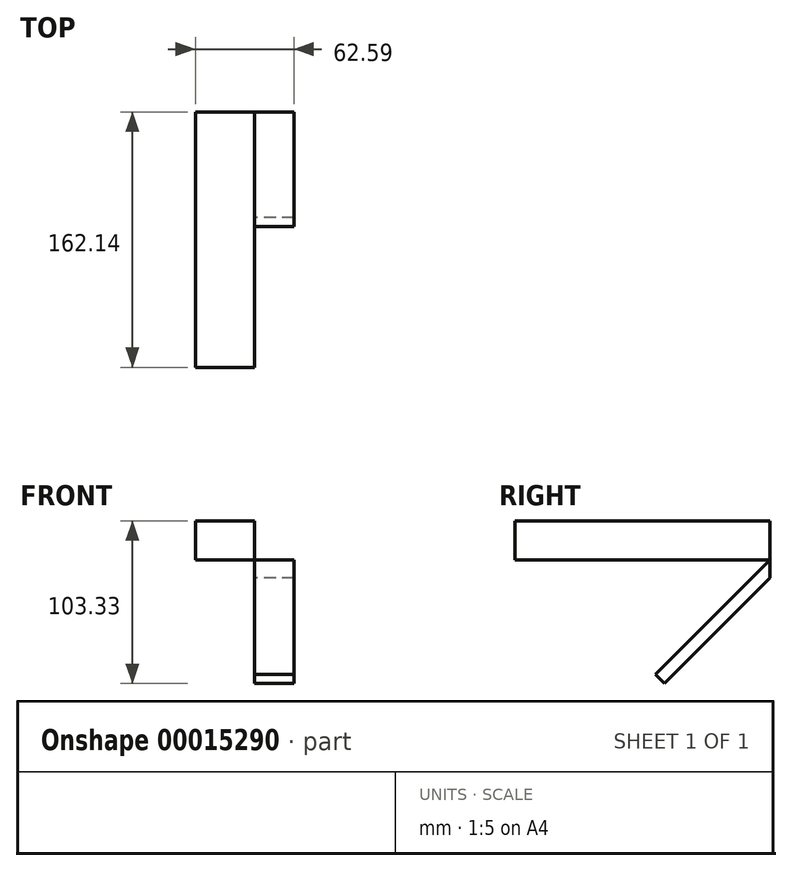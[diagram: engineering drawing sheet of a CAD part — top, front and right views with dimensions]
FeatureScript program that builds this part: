
annotation { "Feature Type Name" : "Feature", "Feature Type Description" : "" }
export const myFeature = defineFeature(function(context is Context, id is Id, definition is map)
    precondition{}
    {
        {
            var Q0;
            Q0=qCreatedBy(makeId("Right.planeOp"),FACE);
            var sketch = newSketch(context, id + "F0", { "sketchPlane" : qUnion([Q0])});
            skLineSegment(sketch, "E0", {"start": v(0, 0) * mm, "end": v(-55, -55) * mm});
            skLineSegment(sketch, "E1", {"start": v(0, -11.31) * mm, "end": v(-49.34, -60.66) * mm});
            skLineSegment(sketch, "E2", {"start": v(-55, -55) * mm, "end": v(-49.34, -60.66) * mm});
            skLineSegment(sketch, "E3", {"start": v(0, 0) * mm, "end": v(0, -11.31) * mm});
            skLineSegment(sketch, "E4", {"start": v(0, 0) * mm, "end": v(-66.64, -66.64) * mm, "construction": true});
            skSolve(sketch);
        }
        {
            var Q0;
            Q0=makeQuery(id+"F0.imprint","IMPRINT",FACE,{"disambiguationData":[TD([[makeQuery(id+"F0.imprint","IMPRINT",EDGE,{"derivedFrom":sQuery(id+"F0.wireOp",EDGE,"E0")}),1.0]])]});
            extrude(context, id + "F1", {"entities" : qUnion([Q0]), "depth" : 25 * mm});
        }
        {
            var Q0;
            Q0=makeQuery(id+"F1.opExtrude","SWEPT_FACE",FACE,{"disambiguationData":[OSD([sQuery(id+"F0.wireOp",EDGE,"E2")])]});
            var sketch = newSketch(context, id + "F2", { "sketchPlane" : qUnion([Q0])});
            skCircle(sketch, "E5", {"center": v(0, 0) * mm, "radius": 100 * mm});
            skLineSegment(sketch, "E6", {"start": v(0, -8) * mm, "end": v(0, -100) * mm});
            skSolve(sketch);
        }
        {
            var Q0;
            Q0=qCreatedBy(makeId("Top.planeOp"),FACE);
            var sketch = newSketch(context, id + "F3", { "sketchPlane" : qUnion([Q0])});
            skLineSegment(sketch, "E7.bottom", {"start": v(0, 0) * mm, "end": v(-37.59, 0) * mm});
            skLineSegment(sketch, "E7.top", {"start": v(0, -162.14) * mm, "end": v(-37.59, -162.14) * mm});
            skLineSegment(sketch, "E7.left", {"start": v(0, 0) * mm, "end": v(0, -162.14) * mm});
            skLineSegment(sketch, "E7.right", {"start": v(-37.59, 0) * mm, "end": v(-37.59, -162.14) * mm});
            skSolve(sketch);
        }
        {
            var Q0;
            Q0 = qSketchRegion(id + "F3", true);
            extrude(context, id + "F4", {"entities" : qUnion([Q0]), "depth" : 25 * mm});
        }
        {
            var Q0;
            {var subQ0=sQuery(id+"F0.wireOp",EDGE,"E2");Q0=makeQuery(id+"F2.imprint","IMPRINT",FACE,{"disambiguationData":[TD([[makeQuery(id+"F2.imprint","IMPRINT",EDGE,{"derivedFrom":makeQuery(id+"F1.opExtrude","CAP_EDGE",EDGE,{"disambiguationData":[OSD([subQ0])],"isStart":true})}),1.0]])]});}
            extrude(context, id + "F5", {"entities" : qUnion([Q0]), "operationType" : NewBodyOperationType.ADD, "depth" : 25 * mm});
        }
    });
